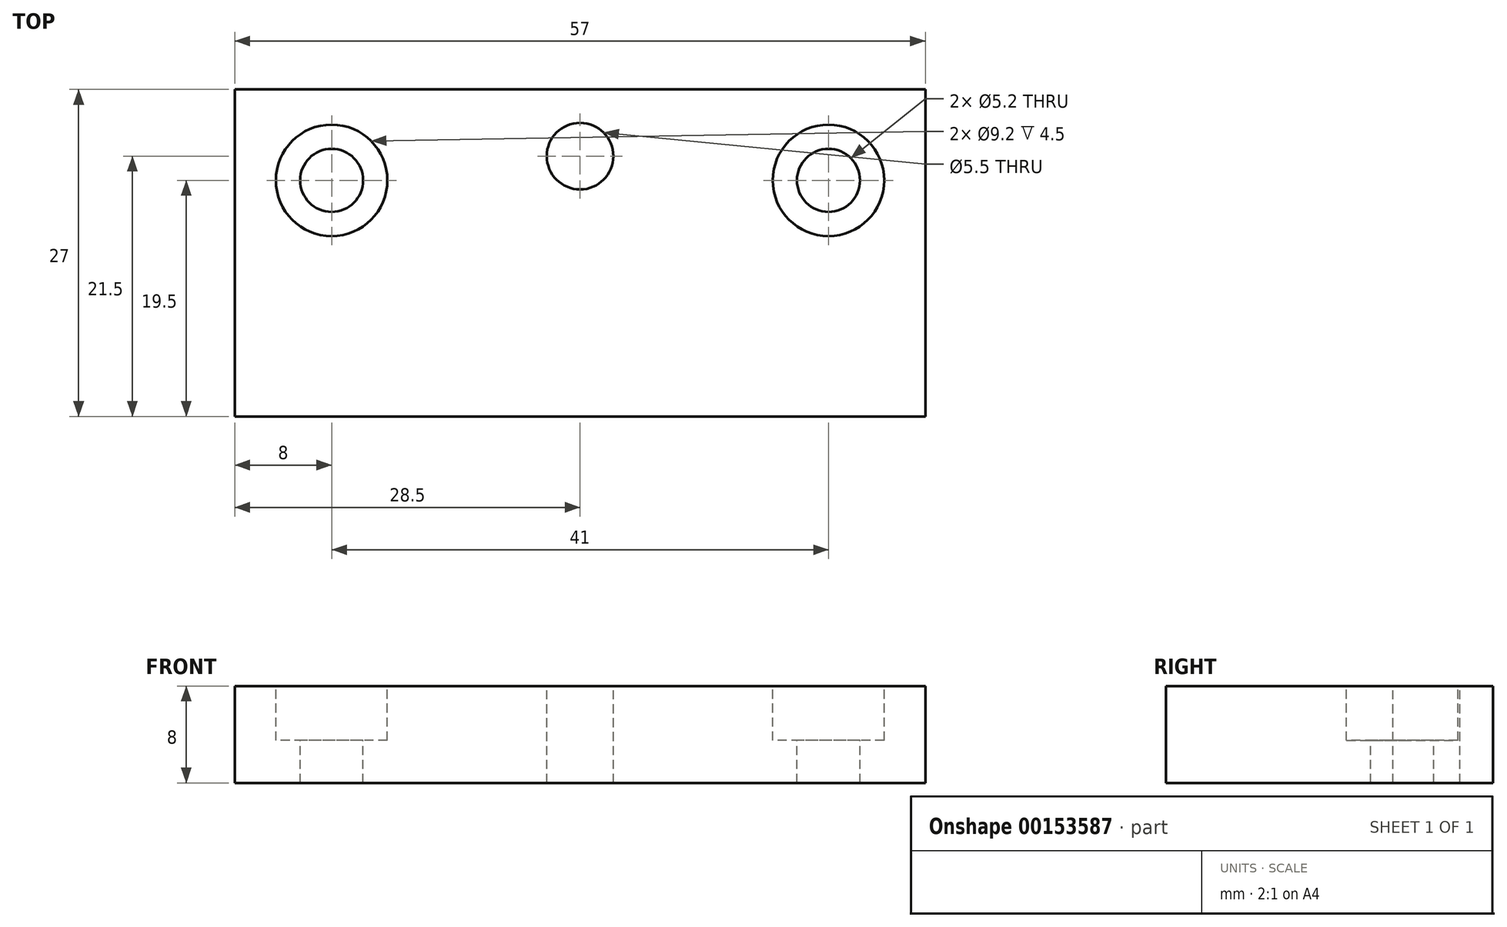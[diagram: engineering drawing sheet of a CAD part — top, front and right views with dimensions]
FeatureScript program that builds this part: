
annotation { "Feature Type Name" : "Feature", "Feature Type Description" : "" }
export const myFeature = defineFeature(function(context is Context, id is Id, definition is map)
    precondition{}
    {
        {
            var Q0;
            Q0=qCreatedBy(makeId("Top.planeOp"),FACE);
            var sketch = newSketch(context, id + "F0", { "sketchPlane" : qUnion([Q0])});
            skLineSegment(sketch, "E0.bottom", {"start": v(-28.5, 27) * mm, "end": v(28.5, 27) * mm});
            skLineSegment(sketch, "E0.top", {"start": v(-28.5, 0) * mm, "end": v(28.5, 0) * mm});
            skLineSegment(sketch, "E0.left", {"start": v(-28.5, 27) * mm, "end": v(-28.5, 0) * mm});
            skLineSegment(sketch, "E0.right", {"start": v(28.5, 27) * mm, "end": v(28.5, 0) * mm});
            skSolve(sketch);
        }
        {
            var Q0;
            Q0=makeQuery(id+"F0.imprint","IMPRINT",FACE,{"disambiguationData":[TD([[makeQuery(id+"F0.imprint","IMPRINT",EDGE,{"derivedFrom":sQuery(id+"F0.wireOp",EDGE,"E0.bottom")}),-1.0]])]});
            extrude(context, id + "F1", {"entities" : qUnion([Q0]), "depth" : 8 * mm});
        }
        {
            var Q0;
            Q0=makeQuery(id+"F1.opExtrude","CAP_FACE",FACE,{"disambiguationData":[OSD([sQuery(id+"F0.wireOp",EDGE,"E0.bottom"),sQuery(id+"F0.wireOp",EDGE,"E0.top"),sQuery(id+"F0.wireOp",EDGE,"E0.left"),sQuery(id+"F0.wireOp",EDGE,"E0.right")])],"isStart":false});
            var sketch = newSketch(context, id + "F2", { "sketchPlane" : qUnion([Q0])});
            skCircle(sketch, "E1", {"center": v(-20.5, 19.5) * mm, "radius": 4.6 * mm});
            skCircle(sketch, "E2", {"center": v(20.5, 19.5) * mm, "radius": 4.6 * mm});
            skCircle(sketch, "E3", {"center": v(0, 21.5) * mm, "radius": 2.75 * mm});
            skCircle(sketch, "E4", {"center": v(-20.5, 19.5) * mm, "radius": 2.6 * mm});
            skCircle(sketch, "E5", {"center": v(20.5, 19.5) * mm, "radius": 2.6 * mm});
            skSolve(sketch);
        }
        {
            var Q0;
            Q0=makeQuery(id+"F2.imprint","IMPRINT",FACE,{"disambiguationData":[TD([[makeQuery(id+"F2.imprint","IMPRINT",EDGE,{"derivedFrom":sQuery(id+"F2.wireOp",EDGE,"E3")}),1.0]])]});
            var Q1;
            Q1=makeQuery(id+"F2.imprint","IMPRINT",FACE,{"disambiguationData":[TD([[makeQuery(id+"F2.imprint","IMPRINT",EDGE,{"derivedFrom":sQuery(id+"F2.wireOp",EDGE,"E5")}),1.0]])]});
            var Q2;
            Q2=makeQuery(id+"F2.imprint","IMPRINT",FACE,{"disambiguationData":[TD([[makeQuery(id+"F2.imprint","IMPRINT",EDGE,{"derivedFrom":sQuery(id+"F2.wireOp",EDGE,"E4")}),1.0]])]});
            extrude(context, id + "F3", {"entities" : qUnion([Q0, Q1, Q2]), "operationType" : NewBodyOperationType.REMOVE, "oppositeDirection" : true, "depth" : 9 * mm});
        }
        {
            var Q0;
            Q0 = qSketchRegion(id + "F2", true);
            extrude(context, id + "F4", {"entities" : qUnion([Q0]), "operationType" : NewBodyOperationType.REMOVE, "oppositeDirection" : true, "depth" : 4.5 * mm});
        }
    });
